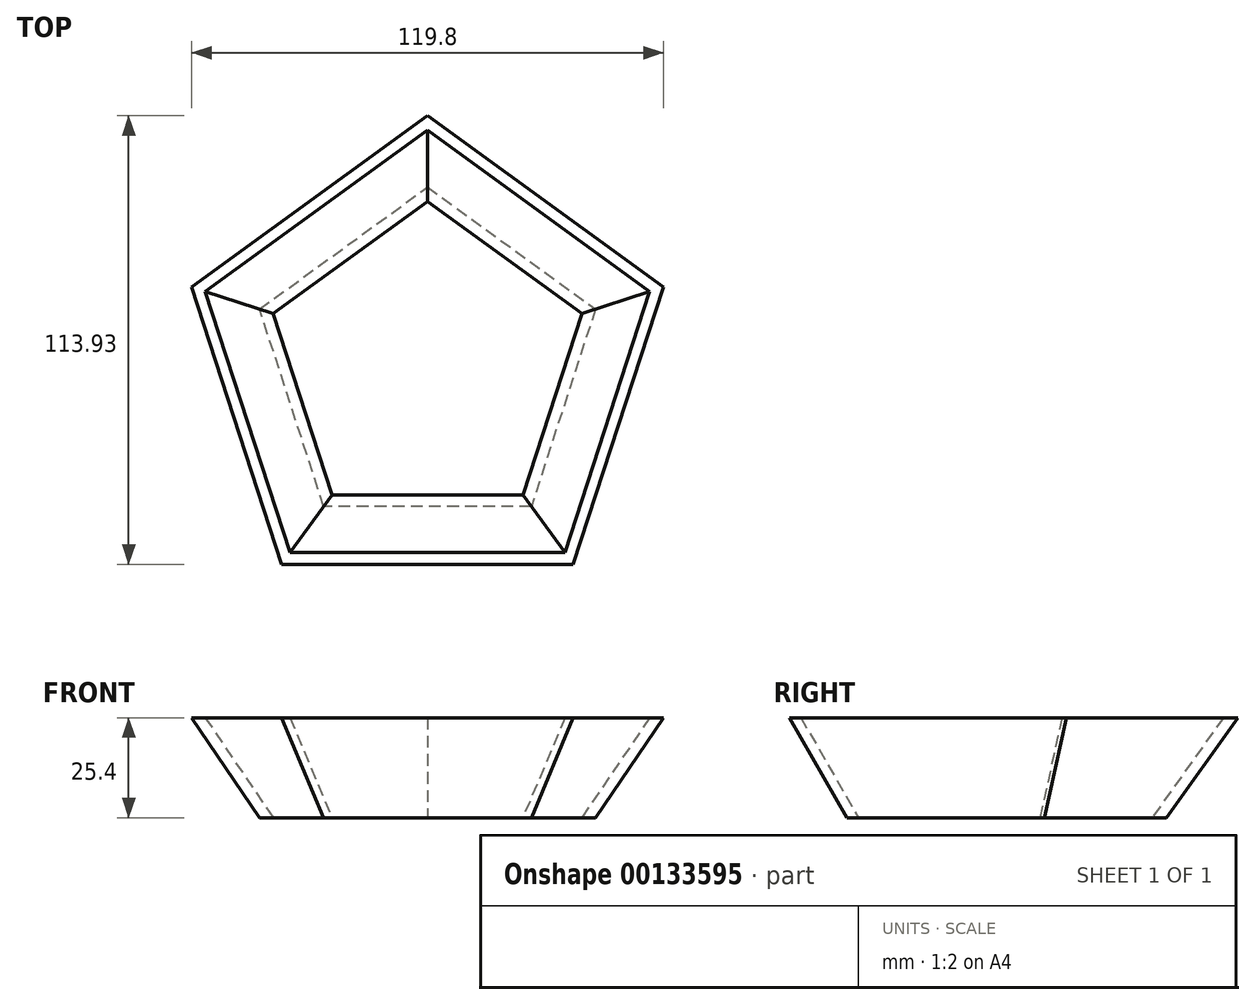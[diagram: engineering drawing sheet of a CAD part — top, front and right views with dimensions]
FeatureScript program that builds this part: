
annotation { "Feature Type Name" : "Feature", "Feature Type Description" : "" }
export const myFeature = defineFeature(function(context is Context, id is Id, definition is map)
    precondition{}
    {
        {
            var Q0;
            Q0=qCreatedBy(makeId("Top.planeOp"),FACE);
            var sketch = newSketch(context, id + "F0", { "sketchPlane" : qUnion([Q0])});
            skCircle(sketch, "E0.cCircle", {"center": v(0, 0) * mm, "radius": 36.29 * mm, "construction": true});
            skLineSegment(sketch, "E0.0", {"start": v(26.37, -36.29) * mm, "end": v(-26.37, -36.29) * mm});
            skLineSegment(sketch, "E0.1", {"start": v(-26.37, -36.29) * mm, "end": v(-42.66, 13.86) * mm});
            skLineSegment(sketch, "E0.2", {"start": v(-42.66, 13.86) * mm, "end": v(0, 44.86) * mm});
            skLineSegment(sketch, "E0.3", {"start": v(0, 44.86) * mm, "end": v(42.66, 13.86) * mm});
            skLineSegment(sketch, "E0.4", {"start": v(42.66, 13.86) * mm, "end": v(26.37, -36.29) * mm});
            skPoint(sketch, "E0.0.midPoint", {"position": v(0, -36.29) * mm});
            skSolve(sketch);
        }
        {
            var Q0;
            Q0=makeQuery(id+"F0.imprint","IMPRINT",FACE,{"disambiguationData":[TD([[makeQuery(id+"F0.imprint","IMPRINT",EDGE,{"derivedFrom":sQuery(id+"F0.wireOp",EDGE,"E0.0")}),-1.0]])]});
            extrude(context, id + "F1", {"entities" : qUnion([Q0]), "depth" : 25.4 * mm, "hasDraft" : true, "draftAngle" : 30 * degree});
        }
        {
            var Q0;
            Q0=makeQuery(id+"F1.opExtrude","CAP_FACE",FACE,{"disambiguationData":[OSD([sQuery(id+"F0.wireOp",EDGE,"E0.0"),sQuery(id+"F0.wireOp",EDGE,"E0.1"),sQuery(id+"F0.wireOp",EDGE,"E0.2"),sQuery(id+"F0.wireOp",EDGE,"E0.3"),sQuery(id+"F0.wireOp",EDGE,"E0.4")])],"isStart":false});
            var Q1;
            Q1=makeQuery(id+"F1.opExtrude","CAP_FACE",FACE,{"disambiguationData":[OSD([sQuery(id+"F0.wireOp",EDGE,"E0.0"),sQuery(id+"F0.wireOp",EDGE,"E0.1"),sQuery(id+"F0.wireOp",EDGE,"E0.2"),sQuery(id+"F0.wireOp",EDGE,"E0.3"),sQuery(id+"F0.wireOp",EDGE,"E0.4")])],"isStart":true});
            shell(context, id + "F2", {"entities" : qUnion([Q0, Q1]), "thickness" : 2.54 * mm});
        }
    });
